# Revit family: for update_56095XXX_new
name_source: partatom
category: Furniture
revit_build: Autodesk Revit 2018 (Build: 20170223_1515(x64)
units: mm (PartAtom-declared; Revit-internal decimal feet)

## family parameters
Cut with Voids When Loaded = Yes
Host = Face
OmniClass Number = 23.31.25.13
OmniClass Title = Bathroom Cabinets
Room Calculation Point = No
Shared = No

## types (6) — shared parameters
BIMobject category = Storage
Description = XtraStoris Individual Wall niche Matt Black with design frame 300/150/100
Design country = Germany
Edition number = 1
IFC Classification = Furnishing Element
Manufacturer = Hansgrohe
Manufacturer country = Germany
Manufacturer name = hansgrohe
Material 1 = Hansgrohe - Metal - Matt Black
Model = 56095XXX
OmniClass Code = 23-31 25 13
OmniClass Description = Bathroom Cabinets
Product Guid = 9da78b48-ae0b-4e43-b4d2-0fb06e61174e
Product SKU = 56095XXX
Product data url = https://bimobject.com
Product family = XtraStoris Individual
Product group = Wall niches
Product name = 56095XXX XtraStoris Individual Wall niche Matt Black with design frame 300/150/100
Product url = https://www.hansgrohe.com
QR code = https://bimobject.com
URL = https://www.hansgrohe.com
Uniclass 2015 Code = Pr_40_20_96_81
Uniclass 2015 Name = Sinks
Weight Net (Kg) = 2.2
zero-valued in all types: Default Elevation

## per-type parameters (varying)
| type | Material 2 |
| 140 Brushed Bronze | Hansgrohe - Metal - 140 Brushed Bronze |
| 340 Brushed Black Chrome | Hansgrohe - Metal - 340 Brushed Black Chrome |
| 670 Matt Black | Hansgrohe - Metal - 670 Matt Black |
| 700 Matt White | Hansgrohe - Metal - 700 Matt White |
| 800 Stainless Steel Optic | Hansgrohe - Metal - 800 Stainless Steel Optic |
| 990 Polished Gold Optic | Hansgrohe - Metal - 990 Polished Gold Optic |

## geometry (parser evidence)
native form markers: Sweep x5
no freeform markers — native parametric forms only
